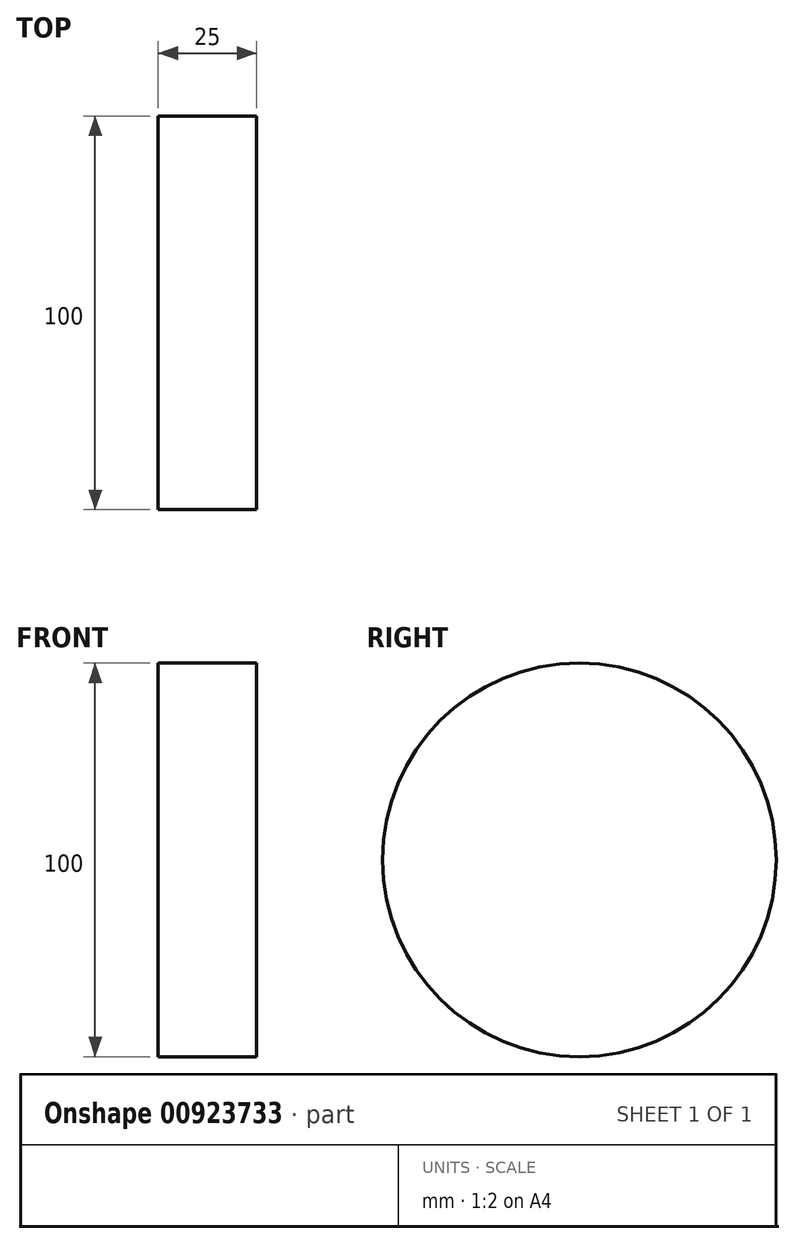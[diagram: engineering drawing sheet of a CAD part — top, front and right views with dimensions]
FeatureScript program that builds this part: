
annotation { "Feature Type Name" : "Feature", "Feature Type Description" : "" }
export const myFeature = defineFeature(function(context is Context, id is Id, definition is map)
    precondition{}
    {
        {
            var Q0;
            Q0=qCreatedBy(makeId("Right.planeOp"),FACE);
            var sketch = newSketch(context, id + "F0", { "sketchPlane" : qUnion([Q0])});
            skEllipse(sketch, "E0", {"center": v(0, 0) * mm, "majorRadius": 50 * mm, "minorRadius": 50 * mm, "majorAxis": v(-1, 0)});
            skSolve(sketch);
        }
        {
            var Q0;
            Q0=makeQuery(id+"F0.imprint","IMPRINT",FACE,{"disambiguationData":[TD([[makeQuery(id+"F0.imprint","IMPRINT",EDGE,{"derivedFrom":sQuery(id+"F0.wireOp",EDGE,"E0")}),1.0]])]});
            extrude(context, id + "F1", {"entities" : qUnion([Q0]), "depth" : 25 * mm, "offsetDistance" : 25 * mm});
        }
    });
